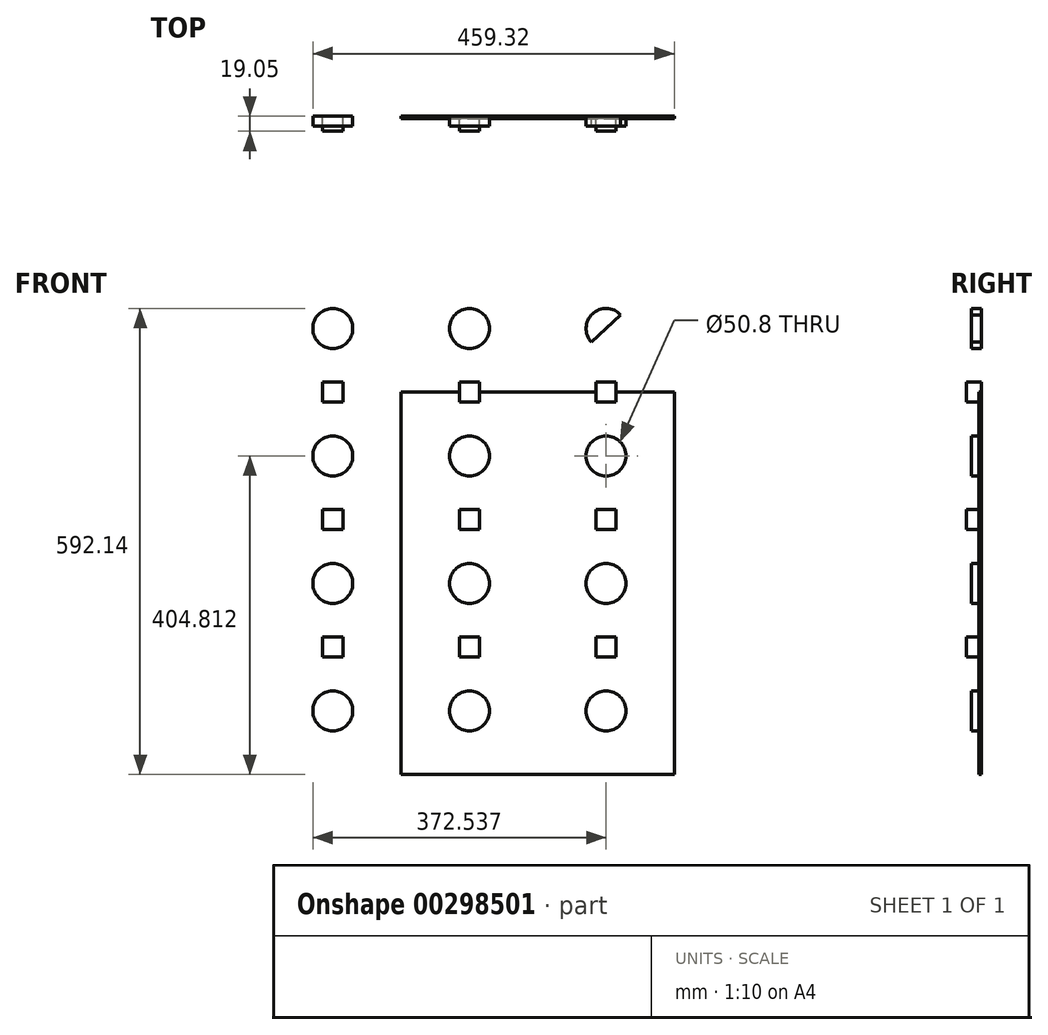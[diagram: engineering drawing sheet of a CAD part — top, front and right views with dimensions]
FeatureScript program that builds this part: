
annotation { "Feature Type Name" : "Feature", "Feature Type Description" : "" }
export const myFeature = defineFeature(function(context is Context, id is Id, definition is map)
    precondition{}
    {
        {
            var Q0;
            Q0=qCreatedBy(makeId("Front.planeOp"),FACE);
            var sketch = newSketch(context, id + "F0", { "sketchPlane" : qUnion([Q0])});
            skLineSegment(sketch, "E0.bottom", {"start": v(-260.35, 323.85) * mm, "end": v(260.35, 323.85) * mm});
            skLineSegment(sketch, "E0.top", {"start": v(-260.35, -323.85) * mm, "end": v(260.35, -323.85) * mm});
            skLineSegment(sketch, "E0.left", {"start": v(-260.35, 323.85) * mm, "end": v(-260.35, -323.85) * mm});
            skLineSegment(sketch, "E0.right", {"start": v(260.35, 323.85) * mm, "end": v(260.35, -323.85) * mm});
            skLineSegment(sketch, "E1", {"start": v(-260.35, 323.85) * mm, "end": v(-86.78, 323.85) * mm});
            skLineSegment(sketch, "E2", {"start": v(-86.78, 323.85) * mm, "end": v(86.78, 323.85) * mm});
            skLineSegment(sketch, "E3", {"start": v(86.78, 323.85) * mm, "end": v(260.35, 323.85) * mm});
            skLineSegment(sketch, "E4", {"start": v(-260.35, 323.85) * mm, "end": v(-260.35, 161.93) * mm});
            skLineSegment(sketch, "E5", {"start": v(-260.35, 161.93) * mm, "end": v(-260.35, 0) * mm});
            skLineSegment(sketch, "E6", {"start": v(-260.35, 0) * mm, "end": v(-260.35, -161.93) * mm});
            skLineSegment(sketch, "E7", {"start": v(-260.35, -161.93) * mm, "end": v(-260.35, -323.85) * mm});
            skLineSegment(sketch, "E8", {"start": v(-86.78, 323.85) * mm, "end": v(-86.78, -323.85) * mm});
            skLineSegment(sketch, "E9", {"start": v(86.78, 323.85) * mm, "end": v(86.78, -323.85) * mm});
            skLineSegment(sketch, "E10", {"start": v(-260.35, 161.93) * mm, "end": v(260.35, 161.93) * mm});
            skLineSegment(sketch, "E11", {"start": v(-260.35, 0) * mm, "end": v(260.35, 0) * mm});
            skLineSegment(sketch, "E12", {"start": v(-260.35, -161.93) * mm, "end": v(260.35, -161.93) * mm});
            skLineSegment(sketch, "E13", {"start": v(-155, 225.56) * mm, "end": v(-192.14, 260.21) * mm});
            skLineSegment(sketch, "E14", {"start": v(0, 242.89) * mm, "end": v(18.57, 225.56) * mm});
            skLineSegment(sketch, "E15", {"start": v(155, 225.56) * mm, "end": v(192.14, 260.21) * mm});
            skLineSegment(sketch, "E16", {"start": v(173.57, 242.89) * mm, "end": v(155, 260.21) * mm});
            skLineSegment(sketch, "E17", {"start": v(-18.57, 225.56) * mm, "end": v(18.57, 260.21) * mm});
            skLineSegment(sketch, "E18", {"start": v(-192.14, 225.56) * mm, "end": v(-155, 260.21) * mm});
            skLineSegment(sketch, "E19", {"start": v(-192.14, 63.64) * mm, "end": v(-155, 98.29) * mm});
            skLineSegment(sketch, "E20", {"start": v(-192.14, 98.29) * mm, "end": v(-155, 63.64) * mm});
            skLineSegment(sketch, "E21", {"start": v(-18.57, 63.64) * mm, "end": v(18.57, 98.29) * mm});
            skLineSegment(sketch, "E22", {"start": v(-18.57, 98.29) * mm, "end": v(18.57, 63.64) * mm});
            skLineSegment(sketch, "E23", {"start": v(155, 63.64) * mm, "end": v(192.14, 98.29) * mm});
            skLineSegment(sketch, "E24", {"start": v(192.14, 63.64) * mm, "end": v(155, 98.29) * mm});
            skLineSegment(sketch, "E25", {"start": v(155, -98.29) * mm, "end": v(192.14, -63.64) * mm});
            skLineSegment(sketch, "E26", {"start": v(192.14, -98.29) * mm, "end": v(155, -63.64) * mm});
            skLineSegment(sketch, "E27", {"start": v(-18.57, -98.29) * mm, "end": v(18.57, -63.64) * mm});
            skLineSegment(sketch, "E28", {"start": v(18.57, -98.29) * mm, "end": v(-18.57, -63.64) * mm});
            skLineSegment(sketch, "E29", {"start": v(-192.14, -98.29) * mm, "end": v(-155, -63.64) * mm});
            skLineSegment(sketch, "E30", {"start": v(-155, -98.29) * mm, "end": v(-192.14, -63.64) * mm});
            skLineSegment(sketch, "E31", {"start": v(-192.14, -260.21) * mm, "end": v(-155, -225.56) * mm});
            skLineSegment(sketch, "E32", {"start": v(-155, -260.21) * mm, "end": v(-192.14, -225.56) * mm});
            skLineSegment(sketch, "E33", {"start": v(-18.57, -225.56) * mm, "end": v(18.57, -260.21) * mm});
            skLineSegment(sketch, "E34", {"start": v(192.14, -225.56) * mm, "end": v(155, -260.21) * mm});
            skLineSegment(sketch, "E35", {"start": v(-18.57, -260.21) * mm, "end": v(18.57, -225.56) * mm});
            skLineSegment(sketch, "E36", {"start": v(192.14, -260.21) * mm, "end": v(155, -225.56) * mm});
            skCircle(sketch, "E37", {"center": v(-173.57, 242.89) * mm, "radius": 25.4 * mm});
            skCircle(sketch, "E38", {"center": v(0, 242.89) * mm, "radius": 25.4 * mm});
            skCircle(sketch, "E39", {"center": v(173.57, 242.89) * mm, "radius": 25.4 * mm});
            skCircle(sketch, "E40", {"center": v(173.57, 80.96) * mm, "radius": 25.4 * mm});
            skPoint(sketch, "E40.centerSnap0", {"position": v(173.57, 80.96) * mm});
            skCircle(sketch, "E41", {"center": v(0, 80.96) * mm, "radius": 25.4 * mm});
            skCircle(sketch, "E42", {"center": v(-173.57, 80.96) * mm, "radius": 25.4 * mm});
            skCircle(sketch, "E43", {"center": v(-173.57, -80.96) * mm, "radius": 25.4 * mm});
            skCircle(sketch, "E44", {"center": v(0, -80.96) * mm, "radius": 25.4 * mm});
            skCircle(sketch, "E45", {"center": v(173.57, -80.96) * mm, "radius": 25.4 * mm});
            skCircle(sketch, "E46", {"center": v(173.57, -242.89) * mm, "radius": 25.4 * mm});
            skCircle(sketch, "E47", {"center": v(0, -242.89) * mm, "radius": 25.4 * mm});
            skCircle(sketch, "E48", {"center": v(-173.57, -242.89) * mm, "radius": 25.4 * mm});
            skPoint(sketch, "E49", {"position": v(-173.57, 161.93) * mm});
            skPoint(sketch, "E50", {"position": v(0, 161.93) * mm});
            skPoint(sketch, "E51", {"position": v(173.57, 161.93) * mm});
            skPoint(sketch, "E52", {"position": v(173.57, 0) * mm});
            skPoint(sketch, "E53", {"position": v(0, 0) * mm});
            skPoint(sketch, "E54", {"position": v(-173.57, 0) * mm});
            skPoint(sketch, "E55", {"position": v(-173.57, -161.93) * mm});
            skPoint(sketch, "E56", {"position": v(0, -161.93) * mm});
            skPoint(sketch, "E57", {"position": v(173.57, -161.93) * mm});
            skLineSegment(sketch, "E58.bottom", {"start": v(-160.87, 149.22) * mm, "end": v(-186.27, 149.22) * mm});
            skLineSegment(sketch, "E58.top", {"start": v(-160.87, 174.62) * mm, "end": v(-186.27, 174.62) * mm});
            skLineSegment(sketch, "E58.left", {"start": v(-160.87, 149.22) * mm, "end": v(-160.87, 174.62) * mm});
            skLineSegment(sketch, "E58.right", {"start": v(-186.27, 149.22) * mm, "end": v(-186.27, 174.63) * mm});
            skLineSegment(sketch, "E59.bottom", {"start": v(12.7, 149.23) * mm, "end": v(-12.7, 149.23) * mm});
            skLineSegment(sketch, "E59.top", {"start": v(12.7, 174.63) * mm, "end": v(-12.7, 174.63) * mm});
            skLineSegment(sketch, "E59.left", {"start": v(12.7, 149.23) * mm, "end": v(12.7, 174.63) * mm});
            skLineSegment(sketch, "E59.right", {"start": v(-12.7, 149.23) * mm, "end": v(-12.7, 174.63) * mm});
            skLineSegment(sketch, "E60.bottom", {"start": v(186.27, 149.23) * mm, "end": v(160.87, 149.23) * mm});
            skLineSegment(sketch, "E60.top", {"start": v(186.27, 174.63) * mm, "end": v(160.87, 174.63) * mm});
            skLineSegment(sketch, "E60.left", {"start": v(186.27, 149.23) * mm, "end": v(186.27, 174.63) * mm});
            skLineSegment(sketch, "E60.right", {"start": v(160.87, 149.23) * mm, "end": v(160.87, 174.63) * mm});
            skLineSegment(sketch, "E61.bottom", {"start": v(186.27, -12.7) * mm, "end": v(160.87, -12.7) * mm});
            skLineSegment(sketch, "E61.top", {"start": v(186.27, 12.7) * mm, "end": v(160.87, 12.7) * mm});
            skLineSegment(sketch, "E61.left", {"start": v(186.27, -12.7) * mm, "end": v(186.27, 12.7) * mm});
            skLineSegment(sketch, "E61.right", {"start": v(160.87, -12.7) * mm, "end": v(160.87, 12.7) * mm});
            skLineSegment(sketch, "E62.bottom", {"start": v(12.7, -12.7) * mm, "end": v(-12.7, -12.7) * mm});
            skLineSegment(sketch, "E62.top", {"start": v(12.7, 12.7) * mm, "end": v(-12.7, 12.7) * mm});
            skLineSegment(sketch, "E62.left", {"start": v(12.7, -12.7) * mm, "end": v(12.7, 12.7) * mm});
            skLineSegment(sketch, "E62.right", {"start": v(-12.7, -12.7) * mm, "end": v(-12.7, 12.7) * mm});
            skLineSegment(sketch, "E63.bottom", {"start": v(-160.87, -12.7) * mm, "end": v(-186.27, -12.7) * mm});
            skLineSegment(sketch, "E63.top", {"start": v(-160.87, 12.7) * mm, "end": v(-186.27, 12.7) * mm});
            skLineSegment(sketch, "E63.left", {"start": v(-160.87, -12.7) * mm, "end": v(-160.87, 12.7) * mm});
            skLineSegment(sketch, "E63.right", {"start": v(-186.27, -12.7) * mm, "end": v(-186.27, 12.7) * mm});
            skLineSegment(sketch, "E64.bottom", {"start": v(-160.87, -174.63) * mm, "end": v(-186.27, -174.63) * mm});
            skLineSegment(sketch, "E64.top", {"start": v(-160.87, -149.23) * mm, "end": v(-186.27, -149.23) * mm});
            skLineSegment(sketch, "E64.left", {"start": v(-160.87, -174.63) * mm, "end": v(-160.87, -149.23) * mm});
            skLineSegment(sketch, "E64.right", {"start": v(-186.27, -174.63) * mm, "end": v(-186.27, -149.23) * mm});
            skLineSegment(sketch, "E65.bottom", {"start": v(12.7, -174.62) * mm, "end": v(-12.7, -174.62) * mm});
            skLineSegment(sketch, "E65.top", {"start": v(12.7, -149.22) * mm, "end": v(-12.7, -149.22) * mm});
            skLineSegment(sketch, "E65.left", {"start": v(12.7, -174.62) * mm, "end": v(12.7, -149.22) * mm});
            skLineSegment(sketch, "E65.right", {"start": v(-12.7, -174.62) * mm, "end": v(-12.7, -149.22) * mm});
            skLineSegment(sketch, "E66.bottom", {"start": v(186.27, -174.62) * mm, "end": v(160.87, -174.62) * mm});
            skLineSegment(sketch, "E66.top", {"start": v(186.27, -149.22) * mm, "end": v(160.87, -149.22) * mm});
            skLineSegment(sketch, "E66.left", {"start": v(186.27, -174.62) * mm, "end": v(186.27, -149.22) * mm});
            skLineSegment(sketch, "E66.right", {"start": v(160.87, -174.62) * mm, "end": v(160.87, -149.22) * mm});
            skPoint(sketch, "E67.orphan", {"position": v(86.78, 161.93) * mm});
            skPoint(sketch, "E68.orphan", {"position": v(-86.78, 0) * mm});
            skPoint(sketch, "E69.orphan", {"position": v(86.78, 0) * mm});
            skPoint(sketch, "E70.orphan", {"position": v(86.78, -161.93) * mm});
            skPoint(sketch, "E71.orphan", {"position": v(-86.78, -161.93) * mm});
            skSolve(sketch);
        }
        {
            var Q0;
            {var subQ13=sQuery(id+"F0.wireOp",EDGE,"E1");Q0=makeQuery(id+"F0.imprint","IMPRINT",FACE,{"disambiguationData":[TD([[makeQuery(id+"F0.imprint","IMPRINT",EDGE,{"derivedFrom":subQ13}),-1.0]])]});}
            var Q1;
            {var subQ13=sQuery(id+"F0.wireOp",EDGE,"E5");Q1=makeQuery(id+"F0.imprint","IMPRINT",FACE,{"disambiguationData":[TD([[makeQuery(id+"F0.imprint","IMPRINT",EDGE,{"derivedFrom":subQ13}),1.0]])]});}
            var Q2;
            {var subQ17=sQuery(id+"F0.wireOp",EDGE,"E59.bottom");Q2=makeQuery(id+"F0.imprint","IMPRINT",FACE,{"disambiguationData":[TD([[makeQuery(id+"F0.imprint","IMPRINT",EDGE,{"derivedFrom":subQ17}),1.0]])]});}
            var Q3;
            {var subQ5=sQuery(id+"F0.wireOp",EDGE,"E2");Q3=makeQuery(id+"F0.imprint","IMPRINT",FACE,{"disambiguationData":[TD([[makeQuery(id+"F0.imprint","IMPRINT",EDGE,{"derivedFrom":subQ5}),-1.0]])]});}
            var Q4;
            {var subQ5=sQuery(id+"F0.wireOp",EDGE,"E3");Q4=makeQuery(id+"F0.imprint","IMPRINT",FACE,{"disambiguationData":[TD([[makeQuery(id+"F0.imprint","IMPRINT",EDGE,{"derivedFrom":subQ5}),-1.0]])]});}
            var Q5;
            {var subQ11=sQuery(id+"F0.wireOp",EDGE,"E61.bottom");Q5=makeQuery(id+"F0.imprint","IMPRINT",FACE,{"disambiguationData":[TD([[makeQuery(id+"F0.imprint","IMPRINT",EDGE,{"derivedFrom":subQ11}),1.0]])]});}
            var Q6;
            {var subQ21=sQuery(id+"F0.wireOp",EDGE,"E60.bottom");Q6=makeQuery(id+"F0.imprint","IMPRINT",FACE,{"disambiguationData":[TD([[makeQuery(id+"F0.imprint","IMPRINT",EDGE,{"derivedFrom":subQ21}),1.0]])]});}
            var Q7;
            {var subQ6=sQuery(id+"F0.wireOp",EDGE,"E62.bottom");Q7=makeQuery(id+"F0.imprint","IMPRINT",FACE,{"disambiguationData":[TD([[makeQuery(id+"F0.imprint","IMPRINT",EDGE,{"derivedFrom":subQ6}),1.0]])]});}
            var Q8;
            {var subQ8=sQuery(id+"F0.wireOp",EDGE,"E6");Q8=makeQuery(id+"F0.imprint","IMPRINT",FACE,{"disambiguationData":[TD([[makeQuery(id+"F0.imprint","IMPRINT",EDGE,{"derivedFrom":subQ8}),1.0]])]});}
            var Q9;
            {var subQ12=sQuery(id+"F0.wireOp",EDGE,"E7");Q9=makeQuery(id+"F0.imprint","IMPRINT",FACE,{"disambiguationData":[TD([[makeQuery(id+"F0.imprint","IMPRINT",EDGE,{"derivedFrom":subQ12}),1.0]])]});}
            var Q10;
            {var subQ0=sQuery(id+"F0.wireOp",EDGE,"E65.bottom");Q10=makeQuery(id+"F0.imprint","IMPRINT",FACE,{"disambiguationData":[TD([[makeQuery(id+"F0.imprint","IMPRINT",EDGE,{"derivedFrom":subQ0}),1.0]])]});}
            var Q11;
            {var subQ17=sQuery(id+"F0.wireOp",EDGE,"E66.bottom");Q11=makeQuery(id+"F0.imprint","IMPRINT",FACE,{"disambiguationData":[TD([[makeQuery(id+"F0.imprint","IMPRINT",EDGE,{"derivedFrom":subQ17}),1.0]])]});}
            extrude(context, id + "F1", {"entities" : qUnion([Q0, Q1, Q2, Q3, Q4, Q5, Q6, Q7, Q8, Q9, Q10, Q11]), "depth" : 3.17 * mm});
        }
        {
            var Q0;
            {var subQ0=sQuery(id+"F0.wireOp",EDGE,"E37");var subQ1=sQuery(id+"F0.wireOp",EDGE,"E13");var subQ2=makeQuery(id+"F0.imprint","INTERSECT",VERTEX,{"disambiguationData":[OD(1.0)],"derivedFrom":[subQ1,subQ0]});Q0=makeQuery(id+"F0.imprint","IMPRINT",FACE,{"disambiguationData":[TD([[makeQuery(id+"F0.imprint","IMPRINT",EDGE,{"disambiguationData":[TD([[subQ2,1.0]])],"derivedFrom":subQ1}),-1.0]])]});}
            var Q1;
            {var subQ0=sQuery(id+"F0.wireOp",EDGE,"E37");var subQ1=sQuery(id+"F0.wireOp",EDGE,"E13");var subQ2=makeQuery(id+"F0.imprint","INTERSECT",VERTEX,{"disambiguationData":[OD(1.0)],"derivedFrom":[subQ1,subQ0]});Q1=makeQuery(id+"F0.imprint","IMPRINT",FACE,{"disambiguationData":[TD([[makeQuery(id+"F0.imprint","IMPRINT",EDGE,{"disambiguationData":[TD([[subQ2,1.0]])],"derivedFrom":subQ1}),1.0]])]});}
            var Q2;
            {var subQ0=sQuery(id+"F0.wireOp",EDGE,"E37");var subQ1=sQuery(id+"F0.wireOp",EDGE,"E13");var subQ2=makeQuery(id+"F0.imprint","INTERSECT",VERTEX,{"disambiguationData":[OD(0.0)],"derivedFrom":[subQ1,subQ0]});Q2=makeQuery(id+"F0.imprint","IMPRINT",FACE,{"disambiguationData":[TD([[makeQuery(id+"F0.imprint","IMPRINT",EDGE,{"disambiguationData":[TD([[subQ2,-1.0]])],"derivedFrom":subQ1}),1.0]])]});}
            var Q3;
            {var subQ0=sQuery(id+"F0.wireOp",EDGE,"E37");var subQ1=sQuery(id+"F0.wireOp",EDGE,"E13");var subQ2=makeQuery(id+"F0.imprint","INTERSECT",VERTEX,{"disambiguationData":[OD(0.0)],"derivedFrom":[subQ1,subQ0]});Q3=makeQuery(id+"F0.imprint","IMPRINT",FACE,{"disambiguationData":[TD([[makeQuery(id+"F0.imprint","IMPRINT",EDGE,{"disambiguationData":[TD([[subQ2,-1.0]])],"derivedFrom":subQ1}),-1.0]])]});}
            var Q4;
            {var subQ0=sQuery(id+"F0.wireOp",EDGE,"E17");var subQ1=makeQuery(id+"F0.imprint","INTERSECT",VERTEX,{"derivedFrom":[sQuery(id+"F0.wireOp",EDGE,"E14"),subQ0]});Q4=makeQuery(id+"F0.imprint","IMPRINT",FACE,{"disambiguationData":[TD([[makeQuery(id+"F0.imprint","IMPRINT",EDGE,{"disambiguationData":[TD([[subQ1,1.0]])],"derivedFrom":subQ0}),1.0]])]});}
            var Q5;
            {var subQ0=sQuery(id+"F0.wireOp",EDGE,"E14");Q5=makeQuery(id+"F0.imprint","IMPRINT",FACE,{"disambiguationData":[TD([[makeQuery(id+"F0.imprint","IMPRINT",EDGE,{"derivedFrom":subQ0}),1.0]])]});}
            var Q6;
            {var subQ0=sQuery(id+"F0.wireOp",EDGE,"E14");Q6=makeQuery(id+"F0.imprint","IMPRINT",FACE,{"disambiguationData":[TD([[makeQuery(id+"F0.imprint","IMPRINT",EDGE,{"derivedFrom":subQ0}),-1.0]])]});}
            var Q7;
            {var subQ3=sQuery(id+"F0.wireOp",EDGE,"E16");Q7=makeQuery(id+"F0.imprint","IMPRINT",FACE,{"disambiguationData":[TD([[makeQuery(id+"F0.imprint","IMPRINT",EDGE,{"derivedFrom":subQ3}),-1.0]])]});}
            var Q8;
            {var subQ3=sQuery(id+"F0.wireOp",EDGE,"E16");Q8=makeQuery(id+"F0.imprint","IMPRINT",FACE,{"disambiguationData":[TD([[makeQuery(id+"F0.imprint","IMPRINT",EDGE,{"derivedFrom":subQ3}),1.0]])]});}
            var Q9;
            {var subQ0=sQuery(id+"F0.wireOp",EDGE,"E39");var subQ1=sQuery(id+"F0.wireOp",EDGE,"E15");var subQ2=makeQuery(id+"F0.imprint","INTERSECT",VERTEX,{"disambiguationData":[OD(0.0)],"derivedFrom":[subQ1,subQ0]});Q9=makeQuery(id+"F0.imprint","IMPRINT",FACE,{"disambiguationData":[TD([[makeQuery(id+"F0.imprint","IMPRINT",EDGE,{"disambiguationData":[TD([[subQ2,-1.0]])],"derivedFrom":subQ1}),-1.0]])]});}
            var Q10;
            {var subQ0=sQuery(id+"F0.wireOp",EDGE,"E40");var subQ1=sQuery(id+"F0.wireOp",EDGE,"E23");var subQ2=makeQuery(id+"F0.imprint","INTERSECT",VERTEX,{"disambiguationData":[OD(1.0)],"derivedFrom":[subQ1,subQ0]});Q10=makeQuery(id+"F0.imprint","IMPRINT",FACE,{"disambiguationData":[TD([[makeQuery(id+"F0.imprint","IMPRINT",EDGE,{"disambiguationData":[TD([[subQ2,1.0]])],"derivedFrom":subQ1}),1.0]])]});}
            var Q11;
            {var subQ0=sQuery(id+"F0.wireOp",EDGE,"E40");var subQ1=sQuery(id+"F0.wireOp",EDGE,"E23");var subQ2=makeQuery(id+"F0.imprint","INTERSECT",VERTEX,{"disambiguationData":[OD(0.0)],"derivedFrom":[subQ1,subQ0]});Q11=makeQuery(id+"F0.imprint","IMPRINT",FACE,{"disambiguationData":[TD([[makeQuery(id+"F0.imprint","IMPRINT",EDGE,{"disambiguationData":[TD([[subQ2,-1.0]])],"derivedFrom":subQ1}),1.0]])]});}
            var Q12;
            {var subQ0=sQuery(id+"F0.wireOp",EDGE,"E40");var subQ1=sQuery(id+"F0.wireOp",EDGE,"E23");var subQ2=makeQuery(id+"F0.imprint","INTERSECT",VERTEX,{"disambiguationData":[OD(0.0)],"derivedFrom":[subQ1,subQ0]});Q12=makeQuery(id+"F0.imprint","IMPRINT",FACE,{"disambiguationData":[TD([[makeQuery(id+"F0.imprint","IMPRINT",EDGE,{"disambiguationData":[TD([[subQ2,-1.0]])],"derivedFrom":subQ1}),-1.0]])]});}
            var Q13;
            {var subQ0=sQuery(id+"F0.wireOp",EDGE,"E40");var subQ1=sQuery(id+"F0.wireOp",EDGE,"E23");var subQ2=makeQuery(id+"F0.imprint","INTERSECT",VERTEX,{"disambiguationData":[OD(1.0)],"derivedFrom":[subQ1,subQ0]});Q13=makeQuery(id+"F0.imprint","IMPRINT",FACE,{"disambiguationData":[TD([[makeQuery(id+"F0.imprint","IMPRINT",EDGE,{"disambiguationData":[TD([[subQ2,1.0]])],"derivedFrom":subQ1}),-1.0]])]});}
            var Q14;
            {var subQ0=sQuery(id+"F0.wireOp",EDGE,"E41");var subQ1=sQuery(id+"F0.wireOp",EDGE,"E21");var subQ2=makeQuery(id+"F0.imprint","INTERSECT",VERTEX,{"disambiguationData":[OD(1.0)],"derivedFrom":[subQ1,subQ0]});Q14=makeQuery(id+"F0.imprint","IMPRINT",FACE,{"disambiguationData":[TD([[makeQuery(id+"F0.imprint","IMPRINT",EDGE,{"disambiguationData":[TD([[subQ2,1.0]])],"derivedFrom":subQ1}),-1.0]])]});}
            var Q15;
            {var subQ0=sQuery(id+"F0.wireOp",EDGE,"E41");var subQ1=sQuery(id+"F0.wireOp",EDGE,"E21");var subQ2=makeQuery(id+"F0.imprint","INTERSECT",VERTEX,{"disambiguationData":[OD(1.0)],"derivedFrom":[subQ1,subQ0]});Q15=makeQuery(id+"F0.imprint","IMPRINT",FACE,{"disambiguationData":[TD([[makeQuery(id+"F0.imprint","IMPRINT",EDGE,{"disambiguationData":[TD([[subQ2,1.0]])],"derivedFrom":subQ1}),1.0]])]});}
            var Q16;
            {var subQ0=sQuery(id+"F0.wireOp",EDGE,"E41");var subQ1=sQuery(id+"F0.wireOp",EDGE,"E21");var subQ2=makeQuery(id+"F0.imprint","INTERSECT",VERTEX,{"disambiguationData":[OD(0.0)],"derivedFrom":[subQ1,subQ0]});Q16=makeQuery(id+"F0.imprint","IMPRINT",FACE,{"disambiguationData":[TD([[makeQuery(id+"F0.imprint","IMPRINT",EDGE,{"disambiguationData":[TD([[subQ2,-1.0]])],"derivedFrom":subQ1}),1.0]])]});}
            var Q17;
            {var subQ0=sQuery(id+"F0.wireOp",EDGE,"E41");var subQ1=sQuery(id+"F0.wireOp",EDGE,"E21");var subQ2=makeQuery(id+"F0.imprint","INTERSECT",VERTEX,{"disambiguationData":[OD(0.0)],"derivedFrom":[subQ1,subQ0]});Q17=makeQuery(id+"F0.imprint","IMPRINT",FACE,{"disambiguationData":[TD([[makeQuery(id+"F0.imprint","IMPRINT",EDGE,{"disambiguationData":[TD([[subQ2,-1.0]])],"derivedFrom":subQ1}),-1.0]])]});}
            var Q18;
            {var subQ0=sQuery(id+"F0.wireOp",EDGE,"E42");var subQ1=sQuery(id+"F0.wireOp",EDGE,"E19");var subQ2=makeQuery(id+"F0.imprint","INTERSECT",VERTEX,{"disambiguationData":[OD(0.0)],"derivedFrom":[subQ1,subQ0]});Q18=makeQuery(id+"F0.imprint","IMPRINT",FACE,{"disambiguationData":[TD([[makeQuery(id+"F0.imprint","IMPRINT",EDGE,{"disambiguationData":[TD([[subQ2,-1.0]])],"derivedFrom":subQ1}),-1.0]])]});}
            var Q19;
            {var subQ0=sQuery(id+"F0.wireOp",EDGE,"E42");var subQ1=sQuery(id+"F0.wireOp",EDGE,"E19");var subQ2=makeQuery(id+"F0.imprint","INTERSECT",VERTEX,{"disambiguationData":[OD(1.0)],"derivedFrom":[subQ1,subQ0]});Q19=makeQuery(id+"F0.imprint","IMPRINT",FACE,{"disambiguationData":[TD([[makeQuery(id+"F0.imprint","IMPRINT",EDGE,{"disambiguationData":[TD([[subQ2,1.0]])],"derivedFrom":subQ1}),-1.0]])]});}
            var Q20;
            {var subQ0=sQuery(id+"F0.wireOp",EDGE,"E42");var subQ1=sQuery(id+"F0.wireOp",EDGE,"E19");var subQ2=makeQuery(id+"F0.imprint","INTERSECT",VERTEX,{"disambiguationData":[OD(1.0)],"derivedFrom":[subQ1,subQ0]});Q20=makeQuery(id+"F0.imprint","IMPRINT",FACE,{"disambiguationData":[TD([[makeQuery(id+"F0.imprint","IMPRINT",EDGE,{"disambiguationData":[TD([[subQ2,1.0]])],"derivedFrom":subQ1}),1.0]])]});}
            var Q21;
            {var subQ0=sQuery(id+"F0.wireOp",EDGE,"E42");var subQ1=sQuery(id+"F0.wireOp",EDGE,"E19");var subQ2=makeQuery(id+"F0.imprint","INTERSECT",VERTEX,{"disambiguationData":[OD(0.0)],"derivedFrom":[subQ1,subQ0]});Q21=makeQuery(id+"F0.imprint","IMPRINT",FACE,{"disambiguationData":[TD([[makeQuery(id+"F0.imprint","IMPRINT",EDGE,{"disambiguationData":[TD([[subQ2,-1.0]])],"derivedFrom":subQ1}),1.0]])]});}
            var Q22;
            {var subQ0=sQuery(id+"F0.wireOp",EDGE,"E43");var subQ1=sQuery(id+"F0.wireOp",EDGE,"E29");var subQ2=makeQuery(id+"F0.imprint","INTERSECT",VERTEX,{"disambiguationData":[OD(1.0)],"derivedFrom":[subQ1,subQ0]});Q22=makeQuery(id+"F0.imprint","IMPRINT",FACE,{"disambiguationData":[TD([[makeQuery(id+"F0.imprint","IMPRINT",EDGE,{"disambiguationData":[TD([[subQ2,1.0]])],"derivedFrom":subQ1}),1.0]])]});}
            var Q23;
            {var subQ0=sQuery(id+"F0.wireOp",EDGE,"E43");var subQ1=sQuery(id+"F0.wireOp",EDGE,"E29");var subQ2=makeQuery(id+"F0.imprint","INTERSECT",VERTEX,{"disambiguationData":[OD(1.0)],"derivedFrom":[subQ1,subQ0]});Q23=makeQuery(id+"F0.imprint","IMPRINT",FACE,{"disambiguationData":[TD([[makeQuery(id+"F0.imprint","IMPRINT",EDGE,{"disambiguationData":[TD([[subQ2,1.0]])],"derivedFrom":subQ1}),-1.0]])]});}
            var Q24;
            {var subQ0=sQuery(id+"F0.wireOp",EDGE,"E43");var subQ1=sQuery(id+"F0.wireOp",EDGE,"E29");var subQ2=makeQuery(id+"F0.imprint","INTERSECT",VERTEX,{"disambiguationData":[OD(0.0)],"derivedFrom":[subQ1,subQ0]});Q24=makeQuery(id+"F0.imprint","IMPRINT",FACE,{"disambiguationData":[TD([[makeQuery(id+"F0.imprint","IMPRINT",EDGE,{"disambiguationData":[TD([[subQ2,-1.0]])],"derivedFrom":subQ1}),-1.0]])]});}
            var Q25;
            {var subQ0=sQuery(id+"F0.wireOp",EDGE,"E43");var subQ1=sQuery(id+"F0.wireOp",EDGE,"E29");var subQ2=makeQuery(id+"F0.imprint","INTERSECT",VERTEX,{"disambiguationData":[OD(0.0)],"derivedFrom":[subQ1,subQ0]});Q25=makeQuery(id+"F0.imprint","IMPRINT",FACE,{"disambiguationData":[TD([[makeQuery(id+"F0.imprint","IMPRINT",EDGE,{"disambiguationData":[TD([[subQ2,-1.0]])],"derivedFrom":subQ1}),1.0]])]});}
            var Q26;
            {var subQ0=sQuery(id+"F0.wireOp",EDGE,"E44");var subQ1=sQuery(id+"F0.wireOp",EDGE,"E27");var subQ2=makeQuery(id+"F0.imprint","INTERSECT",VERTEX,{"disambiguationData":[OD(1.0)],"derivedFrom":[subQ1,subQ0]});Q26=makeQuery(id+"F0.imprint","IMPRINT",FACE,{"disambiguationData":[TD([[makeQuery(id+"F0.imprint","IMPRINT",EDGE,{"disambiguationData":[TD([[subQ2,1.0]])],"derivedFrom":subQ1}),1.0]])]});}
            var Q27;
            {var subQ0=sQuery(id+"F0.wireOp",EDGE,"E44");var subQ1=sQuery(id+"F0.wireOp",EDGE,"E27");var subQ2=makeQuery(id+"F0.imprint","INTERSECT",VERTEX,{"disambiguationData":[OD(0.0)],"derivedFrom":[subQ1,subQ0]});Q27=makeQuery(id+"F0.imprint","IMPRINT",FACE,{"disambiguationData":[TD([[makeQuery(id+"F0.imprint","IMPRINT",EDGE,{"disambiguationData":[TD([[subQ2,-1.0]])],"derivedFrom":subQ1}),1.0]])]});}
            var Q28;
            {var subQ0=sQuery(id+"F0.wireOp",EDGE,"E44");var subQ1=sQuery(id+"F0.wireOp",EDGE,"E27");var subQ2=makeQuery(id+"F0.imprint","INTERSECT",VERTEX,{"disambiguationData":[OD(0.0)],"derivedFrom":[subQ1,subQ0]});Q28=makeQuery(id+"F0.imprint","IMPRINT",FACE,{"disambiguationData":[TD([[makeQuery(id+"F0.imprint","IMPRINT",EDGE,{"disambiguationData":[TD([[subQ2,-1.0]])],"derivedFrom":subQ1}),-1.0]])]});}
            var Q29;
            {var subQ0=sQuery(id+"F0.wireOp",EDGE,"E44");var subQ1=sQuery(id+"F0.wireOp",EDGE,"E27");var subQ2=makeQuery(id+"F0.imprint","INTERSECT",VERTEX,{"disambiguationData":[OD(1.0)],"derivedFrom":[subQ1,subQ0]});Q29=makeQuery(id+"F0.imprint","IMPRINT",FACE,{"disambiguationData":[TD([[makeQuery(id+"F0.imprint","IMPRINT",EDGE,{"disambiguationData":[TD([[subQ2,1.0]])],"derivedFrom":subQ1}),-1.0]])]});}
            var Q30;
            {var subQ0=sQuery(id+"F0.wireOp",EDGE,"E45");var subQ1=sQuery(id+"F0.wireOp",EDGE,"E25");var subQ2=makeQuery(id+"F0.imprint","INTERSECT",VERTEX,{"disambiguationData":[OD(1.0)],"derivedFrom":[subQ1,subQ0]});Q30=makeQuery(id+"F0.imprint","IMPRINT",FACE,{"disambiguationData":[TD([[makeQuery(id+"F0.imprint","IMPRINT",EDGE,{"disambiguationData":[TD([[subQ2,1.0]])],"derivedFrom":subQ1}),1.0]])]});}
            var Q31;
            {var subQ0=sQuery(id+"F0.wireOp",EDGE,"E45");var subQ1=sQuery(id+"F0.wireOp",EDGE,"E25");var subQ2=makeQuery(id+"F0.imprint","INTERSECT",VERTEX,{"disambiguationData":[OD(0.0)],"derivedFrom":[subQ1,subQ0]});Q31=makeQuery(id+"F0.imprint","IMPRINT",FACE,{"disambiguationData":[TD([[makeQuery(id+"F0.imprint","IMPRINT",EDGE,{"disambiguationData":[TD([[subQ2,-1.0]])],"derivedFrom":subQ1}),1.0]])]});}
            var Q32;
            {var subQ0=sQuery(id+"F0.wireOp",EDGE,"E45");var subQ1=sQuery(id+"F0.wireOp",EDGE,"E25");var subQ2=makeQuery(id+"F0.imprint","INTERSECT",VERTEX,{"disambiguationData":[OD(0.0)],"derivedFrom":[subQ1,subQ0]});Q32=makeQuery(id+"F0.imprint","IMPRINT",FACE,{"disambiguationData":[TD([[makeQuery(id+"F0.imprint","IMPRINT",EDGE,{"disambiguationData":[TD([[subQ2,-1.0]])],"derivedFrom":subQ1}),-1.0]])]});}
            var Q33;
            {var subQ0=sQuery(id+"F0.wireOp",EDGE,"E45");var subQ1=sQuery(id+"F0.wireOp",EDGE,"E25");var subQ2=makeQuery(id+"F0.imprint","INTERSECT",VERTEX,{"disambiguationData":[OD(1.0)],"derivedFrom":[subQ1,subQ0]});Q33=makeQuery(id+"F0.imprint","IMPRINT",FACE,{"disambiguationData":[TD([[makeQuery(id+"F0.imprint","IMPRINT",EDGE,{"disambiguationData":[TD([[subQ2,1.0]])],"derivedFrom":subQ1}),-1.0]])]});}
            var Q34;
            {var subQ0=sQuery(id+"F0.wireOp",EDGE,"E46");var subQ1=sQuery(id+"F0.wireOp",EDGE,"E34");var subQ2=makeQuery(id+"F0.imprint","INTERSECT",VERTEX,{"disambiguationData":[OD(0.0)],"derivedFrom":[subQ1,subQ0]});Q34=makeQuery(id+"F0.imprint","IMPRINT",FACE,{"disambiguationData":[TD([[makeQuery(id+"F0.imprint","IMPRINT",EDGE,{"disambiguationData":[TD([[subQ2,-1.0]])],"derivedFrom":subQ1}),-1.0]])]});}
            var Q35;
            {var subQ0=sQuery(id+"F0.wireOp",EDGE,"E46");var subQ1=sQuery(id+"F0.wireOp",EDGE,"E34");var subQ2=makeQuery(id+"F0.imprint","INTERSECT",VERTEX,{"disambiguationData":[OD(1.0)],"derivedFrom":[subQ1,subQ0]});Q35=makeQuery(id+"F0.imprint","IMPRINT",FACE,{"disambiguationData":[TD([[makeQuery(id+"F0.imprint","IMPRINT",EDGE,{"disambiguationData":[TD([[subQ2,1.0]])],"derivedFrom":subQ1}),-1.0]])]});}
            var Q36;
            {var subQ0=sQuery(id+"F0.wireOp",EDGE,"E46");var subQ1=sQuery(id+"F0.wireOp",EDGE,"E34");var subQ2=makeQuery(id+"F0.imprint","INTERSECT",VERTEX,{"disambiguationData":[OD(1.0)],"derivedFrom":[subQ1,subQ0]});Q36=makeQuery(id+"F0.imprint","IMPRINT",FACE,{"disambiguationData":[TD([[makeQuery(id+"F0.imprint","IMPRINT",EDGE,{"disambiguationData":[TD([[subQ2,1.0]])],"derivedFrom":subQ1}),1.0]])]});}
            var Q37;
            {var subQ0=sQuery(id+"F0.wireOp",EDGE,"E46");var subQ1=sQuery(id+"F0.wireOp",EDGE,"E34");var subQ2=makeQuery(id+"F0.imprint","INTERSECT",VERTEX,{"disambiguationData":[OD(0.0)],"derivedFrom":[subQ1,subQ0]});Q37=makeQuery(id+"F0.imprint","IMPRINT",FACE,{"disambiguationData":[TD([[makeQuery(id+"F0.imprint","IMPRINT",EDGE,{"disambiguationData":[TD([[subQ2,-1.0]])],"derivedFrom":subQ1}),1.0]])]});}
            var Q38;
            {var subQ0=sQuery(id+"F0.wireOp",EDGE,"E47");var subQ1=sQuery(id+"F0.wireOp",EDGE,"E33");var subQ2=makeQuery(id+"F0.imprint","INTERSECT",VERTEX,{"disambiguationData":[OD(1.0)],"derivedFrom":[subQ1,subQ0]});Q38=makeQuery(id+"F0.imprint","IMPRINT",FACE,{"disambiguationData":[TD([[makeQuery(id+"F0.imprint","IMPRINT",EDGE,{"disambiguationData":[TD([[subQ2,1.0]])],"derivedFrom":subQ1}),1.0]])]});}
            var Q39;
            {var subQ0=sQuery(id+"F0.wireOp",EDGE,"E47");var subQ1=sQuery(id+"F0.wireOp",EDGE,"E33");var subQ2=makeQuery(id+"F0.imprint","INTERSECT",VERTEX,{"disambiguationData":[OD(1.0)],"derivedFrom":[subQ1,subQ0]});Q39=makeQuery(id+"F0.imprint","IMPRINT",FACE,{"disambiguationData":[TD([[makeQuery(id+"F0.imprint","IMPRINT",EDGE,{"disambiguationData":[TD([[subQ2,1.0]])],"derivedFrom":subQ1}),-1.0]])]});}
            var Q40;
            {var subQ0=sQuery(id+"F0.wireOp",EDGE,"E47");var subQ1=sQuery(id+"F0.wireOp",EDGE,"E33");var subQ2=makeQuery(id+"F0.imprint","INTERSECT",VERTEX,{"disambiguationData":[OD(0.0)],"derivedFrom":[subQ1,subQ0]});Q40=makeQuery(id+"F0.imprint","IMPRINT",FACE,{"disambiguationData":[TD([[makeQuery(id+"F0.imprint","IMPRINT",EDGE,{"disambiguationData":[TD([[subQ2,-1.0]])],"derivedFrom":subQ1}),1.0]])]});}
            var Q41;
            {var subQ0=sQuery(id+"F0.wireOp",EDGE,"E47");var subQ1=sQuery(id+"F0.wireOp",EDGE,"E33");var subQ2=makeQuery(id+"F0.imprint","INTERSECT",VERTEX,{"disambiguationData":[OD(0.0)],"derivedFrom":[subQ1,subQ0]});Q41=makeQuery(id+"F0.imprint","IMPRINT",FACE,{"disambiguationData":[TD([[makeQuery(id+"F0.imprint","IMPRINT",EDGE,{"disambiguationData":[TD([[subQ2,-1.0]])],"derivedFrom":subQ1}),-1.0]])]});}
            var Q42;
            {var subQ0=sQuery(id+"F0.wireOp",EDGE,"E48");var subQ1=sQuery(id+"F0.wireOp",EDGE,"E31");var subQ2=makeQuery(id+"F0.imprint","INTERSECT",VERTEX,{"disambiguationData":[OD(1.0)],"derivedFrom":[subQ1,subQ0]});Q42=makeQuery(id+"F0.imprint","IMPRINT",FACE,{"disambiguationData":[TD([[makeQuery(id+"F0.imprint","IMPRINT",EDGE,{"disambiguationData":[TD([[subQ2,1.0]])],"derivedFrom":subQ1}),-1.0]])]});}
            var Q43;
            {var subQ0=sQuery(id+"F0.wireOp",EDGE,"E48");var subQ1=sQuery(id+"F0.wireOp",EDGE,"E31");var subQ2=makeQuery(id+"F0.imprint","INTERSECT",VERTEX,{"disambiguationData":[OD(0.0)],"derivedFrom":[subQ1,subQ0]});Q43=makeQuery(id+"F0.imprint","IMPRINT",FACE,{"disambiguationData":[TD([[makeQuery(id+"F0.imprint","IMPRINT",EDGE,{"disambiguationData":[TD([[subQ2,-1.0]])],"derivedFrom":subQ1}),-1.0]])]});}
            var Q44;
            {var subQ0=sQuery(id+"F0.wireOp",EDGE,"E48");var subQ1=sQuery(id+"F0.wireOp",EDGE,"E31");var subQ2=makeQuery(id+"F0.imprint","INTERSECT",VERTEX,{"disambiguationData":[OD(0.0)],"derivedFrom":[subQ1,subQ0]});Q44=makeQuery(id+"F0.imprint","IMPRINT",FACE,{"disambiguationData":[TD([[makeQuery(id+"F0.imprint","IMPRINT",EDGE,{"disambiguationData":[TD([[subQ2,-1.0]])],"derivedFrom":subQ1}),1.0]])]});}
            var Q45;
            {var subQ0=sQuery(id+"F0.wireOp",EDGE,"E48");var subQ1=sQuery(id+"F0.wireOp",EDGE,"E31");var subQ2=makeQuery(id+"F0.imprint","INTERSECT",VERTEX,{"disambiguationData":[OD(1.0)],"derivedFrom":[subQ1,subQ0]});Q45=makeQuery(id+"F0.imprint","IMPRINT",FACE,{"disambiguationData":[TD([[makeQuery(id+"F0.imprint","IMPRINT",EDGE,{"disambiguationData":[TD([[subQ2,1.0]])],"derivedFrom":subQ1}),1.0]])]});}
            extrude(context, id + "F2", {"entities" : qUnion([Q0, Q1, Q2, Q3, Q4, Q5, Q6, Q7, Q8, Q9, Q10, Q11, Q12, Q13, Q14, Q15, Q16, Q17, Q18, Q19, Q20, Q21, Q22, Q23, Q24, Q25, Q26, Q27, Q28, Q29, Q30, Q31, Q32, Q33, Q34, Q35, Q36, Q37, Q38, Q39, Q40, Q41, Q42, Q43, Q44, Q45]), "operationType" : NewBodyOperationType.ADD, "depth" : 12.7 * mm});
        }
        {
            var Q0;
            {var subQ5=sQuery(id+"F0.wireOp",EDGE,"E58.top");Q0=makeQuery(id+"F0.imprint","IMPRINT",FACE,{"disambiguationData":[TD([[makeQuery(id+"F0.imprint","IMPRINT",EDGE,{"derivedFrom":subQ5}),1.0]])]});}
            var Q1;
            {var subQ5=sQuery(id+"F0.wireOp",EDGE,"E58.bottom");Q1=makeQuery(id+"F0.imprint","IMPRINT",FACE,{"disambiguationData":[TD([[makeQuery(id+"F0.imprint","IMPRINT",EDGE,{"derivedFrom":subQ5}),-1.0]])]});}
            var Q2;
            {var subQ5=sQuery(id+"F0.wireOp",EDGE,"E59.top");Q2=makeQuery(id+"F0.imprint","IMPRINT",FACE,{"disambiguationData":[TD([[makeQuery(id+"F0.imprint","IMPRINT",EDGE,{"derivedFrom":subQ5}),1.0]])]});}
            var Q3;
            {var subQ5=sQuery(id+"F0.wireOp",EDGE,"E59.bottom");Q3=makeQuery(id+"F0.imprint","IMPRINT",FACE,{"disambiguationData":[TD([[makeQuery(id+"F0.imprint","IMPRINT",EDGE,{"derivedFrom":subQ5}),-1.0]])]});}
            var Q4;
            {var subQ5=sQuery(id+"F0.wireOp",EDGE,"E60.top");Q4=makeQuery(id+"F0.imprint","IMPRINT",FACE,{"disambiguationData":[TD([[makeQuery(id+"F0.imprint","IMPRINT",EDGE,{"derivedFrom":subQ5}),1.0]])]});}
            var Q5;
            {var subQ5=sQuery(id+"F0.wireOp",EDGE,"E60.bottom");Q5=makeQuery(id+"F0.imprint","IMPRINT",FACE,{"disambiguationData":[TD([[makeQuery(id+"F0.imprint","IMPRINT",EDGE,{"derivedFrom":subQ5}),-1.0]])]});}
            var Q6;
            {var subQ5=sQuery(id+"F0.wireOp",EDGE,"E61.top");Q6=makeQuery(id+"F0.imprint","IMPRINT",FACE,{"disambiguationData":[TD([[makeQuery(id+"F0.imprint","IMPRINT",EDGE,{"derivedFrom":subQ5}),1.0]])]});}
            var Q7;
            {var subQ5=sQuery(id+"F0.wireOp",EDGE,"E61.bottom");Q7=makeQuery(id+"F0.imprint","IMPRINT",FACE,{"disambiguationData":[TD([[makeQuery(id+"F0.imprint","IMPRINT",EDGE,{"derivedFrom":subQ5}),-1.0]])]});}
            var Q8;
            {var subQ5=sQuery(id+"F0.wireOp",EDGE,"E62.top");Q8=makeQuery(id+"F0.imprint","IMPRINT",FACE,{"disambiguationData":[TD([[makeQuery(id+"F0.imprint","IMPRINT",EDGE,{"derivedFrom":subQ5}),1.0]])]});}
            var Q9;
            {var subQ5=sQuery(id+"F0.wireOp",EDGE,"E62.bottom");Q9=makeQuery(id+"F0.imprint","IMPRINT",FACE,{"disambiguationData":[TD([[makeQuery(id+"F0.imprint","IMPRINT",EDGE,{"derivedFrom":subQ5}),-1.0]])]});}
            var Q10;
            {var subQ5=sQuery(id+"F0.wireOp",EDGE,"E63.top");Q10=makeQuery(id+"F0.imprint","IMPRINT",FACE,{"disambiguationData":[TD([[makeQuery(id+"F0.imprint","IMPRINT",EDGE,{"derivedFrom":subQ5}),1.0]])]});}
            var Q11;
            {var subQ5=sQuery(id+"F0.wireOp",EDGE,"E63.bottom");Q11=makeQuery(id+"F0.imprint","IMPRINT",FACE,{"disambiguationData":[TD([[makeQuery(id+"F0.imprint","IMPRINT",EDGE,{"derivedFrom":subQ5}),-1.0]])]});}
            var Q12;
            {var subQ5=sQuery(id+"F0.wireOp",EDGE,"E64.top");Q12=makeQuery(id+"F0.imprint","IMPRINT",FACE,{"disambiguationData":[TD([[makeQuery(id+"F0.imprint","IMPRINT",EDGE,{"derivedFrom":subQ5}),1.0]])]});}
            var Q13;
            {var subQ5=sQuery(id+"F0.wireOp",EDGE,"E64.bottom");Q13=makeQuery(id+"F0.imprint","IMPRINT",FACE,{"disambiguationData":[TD([[makeQuery(id+"F0.imprint","IMPRINT",EDGE,{"derivedFrom":subQ5}),-1.0]])]});}
            var Q14;
            {var subQ5=sQuery(id+"F0.wireOp",EDGE,"E65.top");Q14=makeQuery(id+"F0.imprint","IMPRINT",FACE,{"disambiguationData":[TD([[makeQuery(id+"F0.imprint","IMPRINT",EDGE,{"derivedFrom":subQ5}),1.0]])]});}
            var Q15;
            {var subQ5=sQuery(id+"F0.wireOp",EDGE,"E65.bottom");Q15=makeQuery(id+"F0.imprint","IMPRINT",FACE,{"disambiguationData":[TD([[makeQuery(id+"F0.imprint","IMPRINT",EDGE,{"derivedFrom":subQ5}),-1.0]])]});}
            var Q16;
            {var subQ5=sQuery(id+"F0.wireOp",EDGE,"E66.top");Q16=makeQuery(id+"F0.imprint","IMPRINT",FACE,{"disambiguationData":[TD([[makeQuery(id+"F0.imprint","IMPRINT",EDGE,{"derivedFrom":subQ5}),1.0]])]});}
            var Q17;
            {var subQ5=sQuery(id+"F0.wireOp",EDGE,"E66.bottom");Q17=makeQuery(id+"F0.imprint","IMPRINT",FACE,{"disambiguationData":[TD([[makeQuery(id+"F0.imprint","IMPRINT",EDGE,{"derivedFrom":subQ5}),-1.0]])]});}
            extrude(context, id + "F3", {"entities" : qUnion([Q0, Q1, Q2, Q3, Q4, Q5, Q6, Q7, Q8, Q9, Q10, Q11, Q12, Q13, Q14, Q15, Q16, Q17]), "operationType" : NewBodyOperationType.ADD, "depth" : 19.05 * mm});
        }
    });
